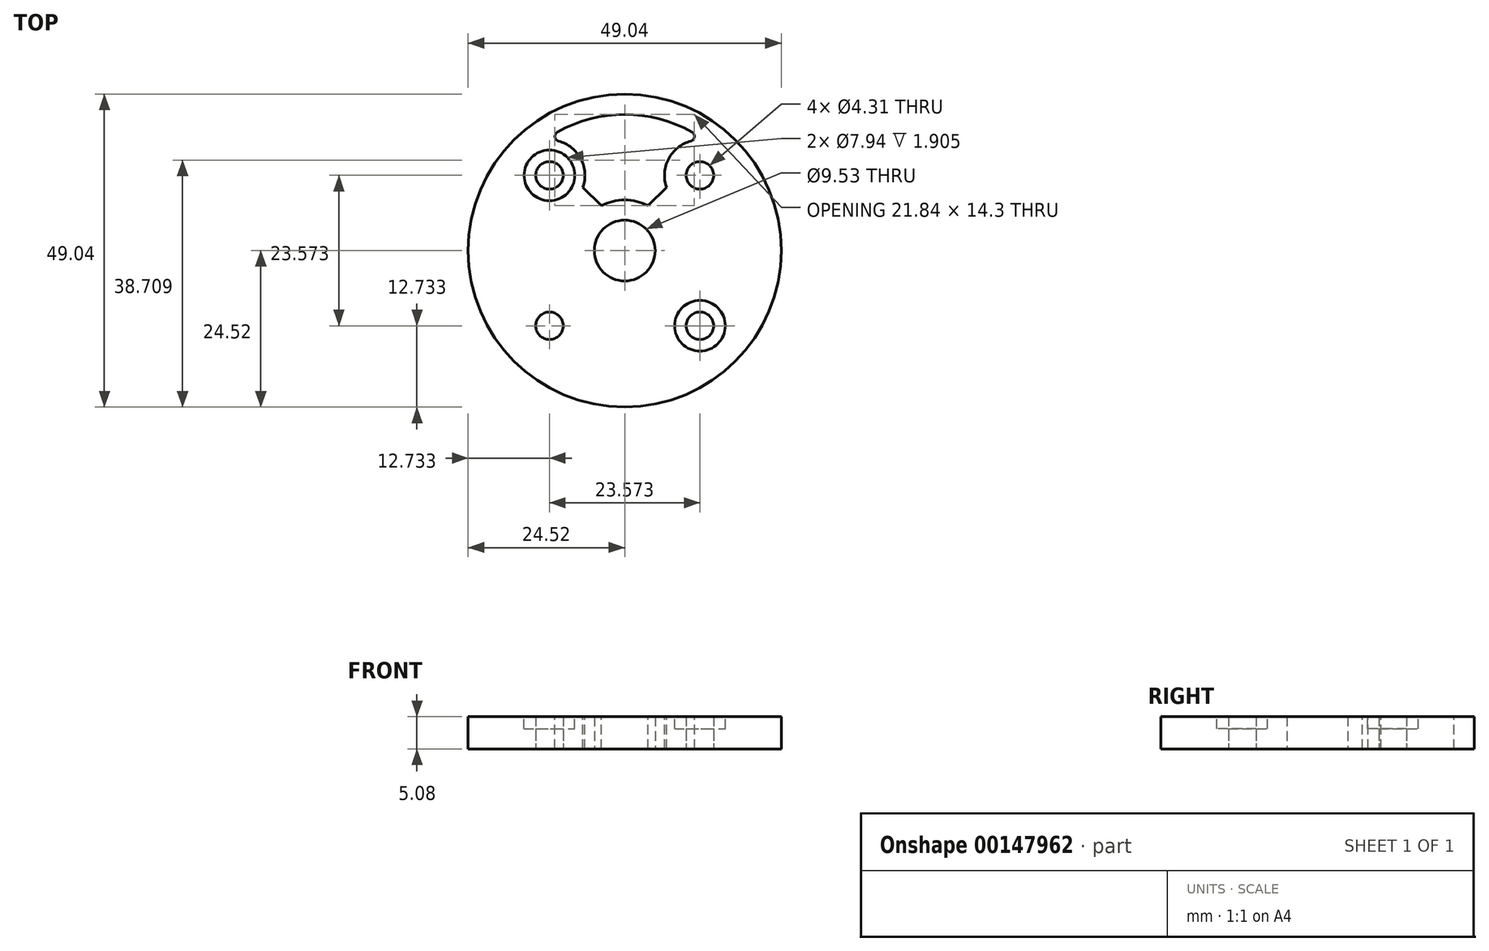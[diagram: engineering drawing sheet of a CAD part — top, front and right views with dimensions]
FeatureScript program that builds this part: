
annotation { "Feature Type Name" : "Feature", "Feature Type Description" : "" }
export const myFeature = defineFeature(function(context is Context, id is Id, definition is map)
    precondition{}
    {
        {
            var Q0;
            Q0=qCreatedBy(makeId("Top.planeOp"),FACE);
            var sketch = newSketch(context, id + "F0", { "sketchPlane" : qUnion([Q0])});
            skCircle(sketch, "E0", {"center": v(0, 0) * mm, "radius": 24.52 * mm});
            skCircle(sketch, "E1", {"center": v(0, 0) * mm, "radius": 4.76 * mm});
            skLineSegment(sketch, "E2.bottom", {"start": v(-11.79, 11.79) * mm, "end": v(11.79, 11.79) * mm, "construction": true});
            skLineSegment(sketch, "E2.top", {"start": v(-11.79, -11.79) * mm, "end": v(11.79, -11.79) * mm, "construction": true});
            skLineSegment(sketch, "E2.left", {"start": v(-11.79, 11.79) * mm, "end": v(-11.79, -11.79) * mm, "construction": true});
            skLineSegment(sketch, "E2.right", {"start": v(11.79, 11.79) * mm, "end": v(11.79, -11.79) * mm, "construction": true});
            skCircle(sketch, "E3", {"center": v(-11.79, 11.79) * mm, "radius": 7.85 * mm, "construction": true});
            skCircle(sketch, "E4", {"center": v(11.79, 11.79) * mm, "radius": 2.15 * mm});
            skCircle(sketch, "E5", {"center": v(-11.79, 11.79) * mm, "radius": 2.15 * mm});
            skCircle(sketch, "E6", {"center": v(-11.79, -11.79) * mm, "radius": 2.15 * mm});
            skCircle(sketch, "E7", {"center": v(11.79, -11.79) * mm, "radius": 2.15 * mm});
            skCircle(sketch, "E8", {"center": v(-11.79, -11.79) * mm, "radius": 3.97 * mm, "construction": true});
            skCircle(sketch, "E9", {"center": v(11.79, 11.79) * mm, "radius": 3.97 * mm, "construction": true});
            skSolve(sketch);
        }
        {
            var Q0;
            Q0=qSketchRegion(id+"F0",true);
            extrude(context, id + "F1", {"entities" : qUnion([Q0]), "depth" : 5.08 * mm});
        }
        {
            var Q0;
            Q0=makeQuery(id+"F1.opExtrude","CAP_FACE",FACE,{"disambiguationData":[OSD([sQuery(id+"F0.wireOp",EDGE,"E0"),sQuery(id+"F0.wireOp",EDGE,"E1"),sQuery(id+"F0.wireOp",EDGE,"E4"),sQuery(id+"F0.wireOp",EDGE,"E5"),sQuery(id+"F0.wireOp",EDGE,"E6"),sQuery(id+"F0.wireOp",EDGE,"E7")])],"isStart":false});
            var sketch = newSketch(context, id + "F2", { "sketchPlane" : qUnion([Q0])});
            skArc(sketch, "E10", {"start": v(-6.55, 9.92) * mm, "mid": v(-7.46, 15.27) * mm, "end": v(-12.5, 17.3) * mm});
            skArc(sketch, "E11", {"start": v(12.5, 17.3) * mm, "mid": v(7.46, 15.27) * mm, "end": v(6.55, 9.92) * mm});
            skArc(sketch, "E12", {"start": v(12.5, 17.3) * mm, "mid": v(0, 21.34) * mm, "end": v(-12.5, 17.3) * mm});
            skArc(sketch, "E13", {"start": v(3.67, 7.04) * mm, "mid": v(0, 7.94) * mm, "end": v(-3.67, 7.04) * mm});
            skLineSegment(sketch, "E14.bottom", {"start": v(-9.92, 6.55) * mm, "end": v(-6.55, 9.92) * mm, "construction": true});
            skLineSegment(sketch, "E14.top", {"start": v(-7.04, 3.67) * mm, "end": v(-3.67, 7.04) * mm, "construction": true});
            skLineSegment(sketch, "E14.left", {"start": v(-9.92, 6.55) * mm, "end": v(-7.04, 3.67) * mm, "construction": true});
            skLineSegment(sketch, "E14.right", {"start": v(-6.55, 9.92) * mm, "end": v(-3.67, 7.04) * mm});
            skLineSegment(sketch, "E15.bottom", {"start": v(9.92, 6.55) * mm, "end": v(6.55, 9.92) * mm, "construction": true});
            skLineSegment(sketch, "E15.top", {"start": v(7.04, 3.67) * mm, "end": v(3.67, 7.04) * mm, "construction": true});
            skLineSegment(sketch, "E15.left", {"start": v(9.92, 6.55) * mm, "end": v(7.04, 3.67) * mm, "construction": true});
            skLineSegment(sketch, "E15.right", {"start": v(6.55, 9.92) * mm, "end": v(3.67, 7.04) * mm});
            skLineSegment(sketch, "E16", {"start": v(-8.24, 8.24) * mm, "end": v(-11.79, 11.79) * mm, "construction": true});
            skLineSegment(sketch, "E17", {"start": v(-5.35, 5.35) * mm, "end": v(0, 0) * mm, "construction": true});
            skLineSegment(sketch, "E18", {"start": v(0, 0) * mm, "end": v(5.35, 5.35) * mm, "construction": true});
            skLineSegment(sketch, "E19", {"start": v(8.24, 8.24) * mm, "end": v(11.79, 11.79) * mm, "construction": true});
            skSolve(sketch);
        }
        {
            var Q0;
            Q0=makeQuery(id+"F2.imprint","IMPRINT",FACE,{"disambiguationData":[TD([[makeQuery(id+"F2.imprint","IMPRINT",EDGE,{"derivedFrom":sQuery(id+"F2.wireOp",EDGE,"E10")}),-1.0]])]});
            var Q1;
            Q1=makeQuery(id+"F1.opExtrude","CAP_FACE",FACE,{"disambiguationData":[OSD([sQuery(id+"F0.wireOp",EDGE,"E0"),sQuery(id+"F0.wireOp",EDGE,"E1"),sQuery(id+"F0.wireOp",EDGE,"E4"),sQuery(id+"F0.wireOp",EDGE,"E5"),sQuery(id+"F0.wireOp",EDGE,"E6"),sQuery(id+"F0.wireOp",EDGE,"E7")])],"isStart":true});
            extrude(context, id + "F3", {"entities" : qUnion([Q0]), "operationType" : NewBodyOperationType.REMOVE, "endBound" : BoundingType.UP_TO_SURFACE, "oppositeDirection" : true, "endBoundEntityFace" : qUnion([Q1]), "depth" : 25.4 * mm});
        }
        {
            var Q0;
            Q0=makeQuery(id+"F6MqURjXbY15YYN_1.1.F3.boolean.opBoolean","COPY",EDGE,{"derivedFrom":makeQuery(id+"F6MqURjXbY15YYN_1.1.F3.opExtrude","SWEPT_EDGE",EDGE,{"disambiguationData":[OSD([sQuery(id+"F2.wireOp",EDGE,"E10"),sQuery(id+"F2.wireOp",EDGE,"E12")])]})});
            var Q1;
            Q1=makeQuery(id+"F6MqURjXbY15YYN_1.1.F3.boolean.opBoolean","COPY",EDGE,{"derivedFrom":makeQuery(id+"F6MqURjXbY15YYN_1.1.F3.opExtrude","SWEPT_EDGE",EDGE,{"disambiguationData":[OSD([sQuery(id+"F2.wireOp",EDGE,"E11"),sQuery(id+"F2.wireOp",EDGE,"E12")])]})});
            var Q2;
            Q2=makeQuery(id+"F6MqURjXbY15YYN_1.2.F3.boolean.opBoolean","COPY",EDGE,{"derivedFrom":makeQuery(id+"F6MqURjXbY15YYN_1.2.F3.opExtrude","SWEPT_EDGE",EDGE,{"disambiguationData":[OSD([sQuery(id+"F2.wireOp",EDGE,"E10"),sQuery(id+"F2.wireOp",EDGE,"E12")])]})});
            var Q3;
            Q3=makeQuery(id+"F6MqURjXbY15YYN_1.2.F3.boolean.opBoolean","COPY",EDGE,{"derivedFrom":makeQuery(id+"F6MqURjXbY15YYN_1.2.F3.opExtrude","SWEPT_EDGE",EDGE,{"disambiguationData":[OSD([sQuery(id+"F2.wireOp",EDGE,"E11"),sQuery(id+"F2.wireOp",EDGE,"E12")])]})});
            var Q4;
            Q4=makeQuery(id+"F6MqURjXbY15YYN_1.3.F3.boolean.opBoolean","COPY",EDGE,{"derivedFrom":makeQuery(id+"F6MqURjXbY15YYN_1.3.F3.opExtrude","SWEPT_EDGE",EDGE,{"disambiguationData":[OSD([sQuery(id+"F2.wireOp",EDGE,"E10"),sQuery(id+"F2.wireOp",EDGE,"E12")])]})});
            var Q5;
            Q5=makeQuery(id+"F6MqURjXbY15YYN_1.3.F3.boolean.opBoolean","COPY",EDGE,{"derivedFrom":makeQuery(id+"F6MqURjXbY15YYN_1.3.F3.opExtrude","SWEPT_EDGE",EDGE,{"disambiguationData":[OSD([sQuery(id+"F2.wireOp",EDGE,"E11"),sQuery(id+"F2.wireOp",EDGE,"E12")])]})});
            var Q6;
            Q6=makeQuery(id+"F3.boolean.opBoolean","COPY",EDGE,{"derivedFrom":makeQuery(id+"F3.opExtrude","SWEPT_EDGE",EDGE,{"disambiguationData":[OSD([sQuery(id+"F2.wireOp",EDGE,"E10"),sQuery(id+"F2.wireOp",EDGE,"E12")])]})});
            var Q7;
            Q7=makeQuery(id+"F3.boolean.opBoolean","COPY",EDGE,{"derivedFrom":makeQuery(id+"F3.opExtrude","SWEPT_EDGE",EDGE,{"disambiguationData":[OSD([sQuery(id+"F2.wireOp",EDGE,"E11"),sQuery(id+"F2.wireOp",EDGE,"E12")])]})});
            fillet(context, id + "F4", {"entities" : qUnion([Q0, Q1, Q2, Q3, Q4, Q5, Q6, Q7]), "radius" : 0.76 * mm, "tangentPropagation" : true, "allowEdgeOverflow" : false});
        }
        {
            var Q0;
            Q0=makeQuery(id+"F1.opExtrude","CAP_FACE",FACE,{"disambiguationData":[OSD([sQuery(id+"F0.wireOp",EDGE,"E0"),sQuery(id+"F0.wireOp",EDGE,"E1"),sQuery(id+"F0.wireOp",EDGE,"E4"),sQuery(id+"F0.wireOp",EDGE,"E5"),sQuery(id+"F0.wireOp",EDGE,"E6"),sQuery(id+"F0.wireOp",EDGE,"E7")])],"isStart":true});
            cPlane(context, id + "F5", {"entities" : qUnion([Q0]), "cplaneType" : CPlaneType.OFFSET, "offset" : 3.17 * mm, "oppositeDirection" : true, "width" : 152.4 * mm, "height" : 152.4 * mm});
        }
        {
            var Q0;
            Q0=makeQuery(id+"F1.opExtrude","CAP_FACE",FACE,{"disambiguationData":[OSD([sQuery(id+"F0.wireOp",EDGE,"E0"),sQuery(id+"F0.wireOp",EDGE,"E1"),sQuery(id+"F0.wireOp",EDGE,"E4"),sQuery(id+"F0.wireOp",EDGE,"E5"),sQuery(id+"F0.wireOp",EDGE,"E6"),sQuery(id+"F0.wireOp",EDGE,"E7")])],"isStart":false});
            var sketch = newSketch(context, id + "F6", { "sketchPlane" : qUnion([Q0])});
            skCircle(sketch, "E20", {"center": v(11.79, -11.79) * mm, "radius": 3.97 * mm});
            skCircle(sketch, "E21", {"center": v(-11.79, 11.79) * mm, "radius": 3.97 * mm});
            skSolve(sketch);
        }
        {
            var Q0;
            Q0=qSketchRegion(id+"F6",true);
            var Q1;
            Q1=qCreatedBy(id+"F5.planeOp",FACE);
            extrude(context, id + "F7", {"entities" : qUnion([Q0]), "operationType" : NewBodyOperationType.REMOVE, "endBound" : BoundingType.UP_TO_SURFACE, "oppositeDirection" : true, "endBoundEntityFace" : qUnion([Q1]), "depth" : 25.4 * mm});
        }
    });
